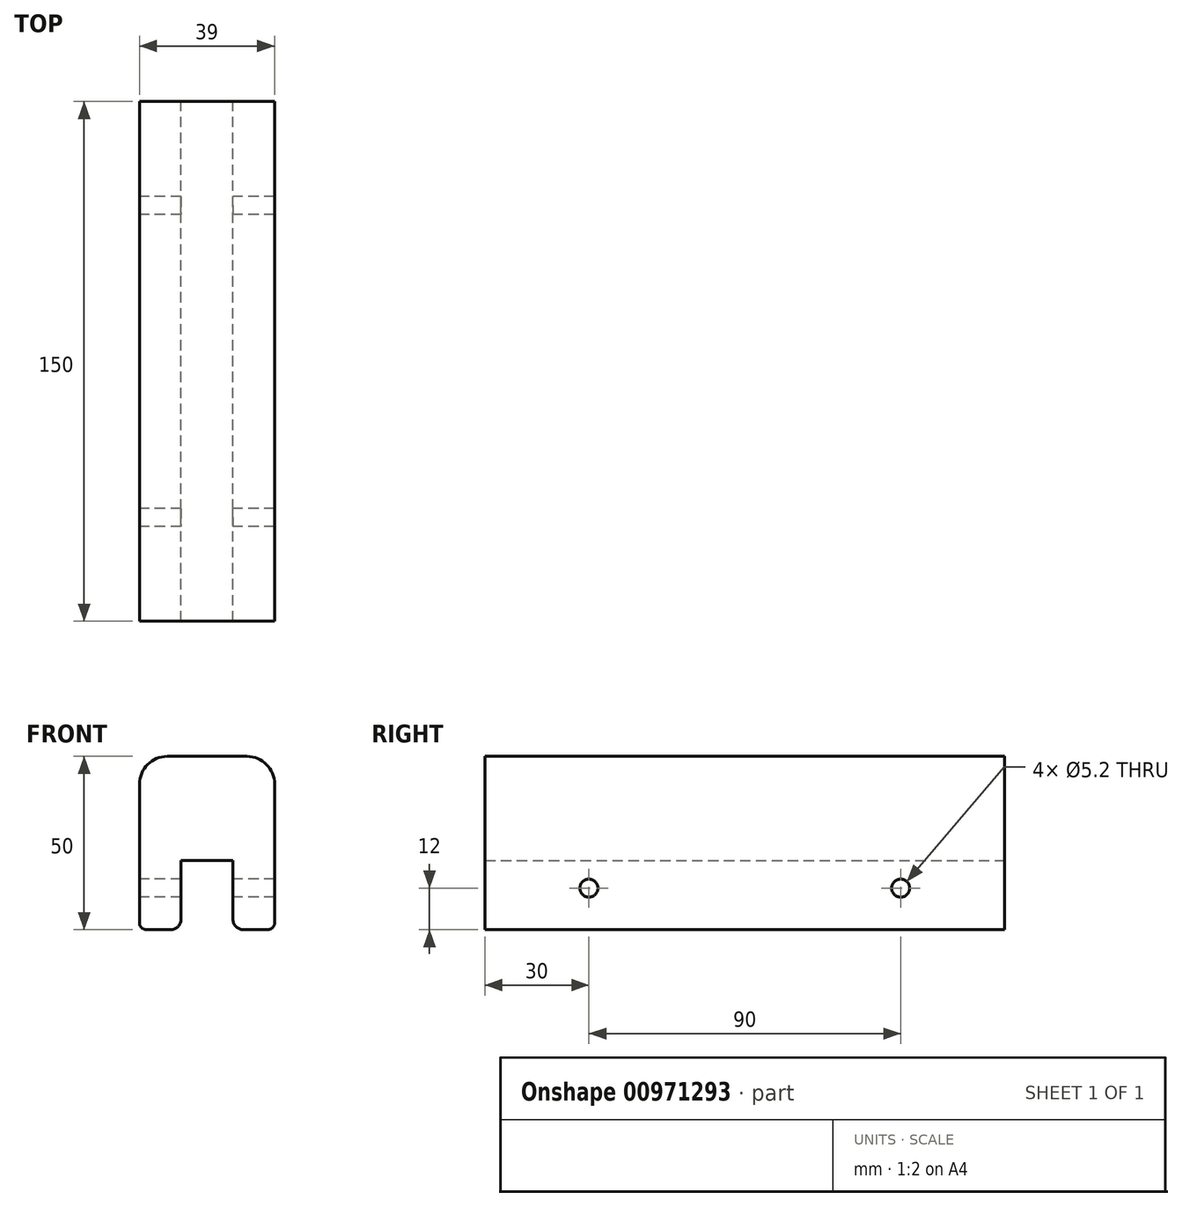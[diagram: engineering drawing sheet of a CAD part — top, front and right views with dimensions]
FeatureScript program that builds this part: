
annotation { "Feature Type Name" : "Feature", "Feature Type Description" : "" }
export const myFeature = defineFeature(function(context is Context, id is Id, definition is map)
    precondition{}
    {
        {
            var Q0;
            Q0=qCreatedBy(makeId("Front.planeOp"),FACE);
            var sketch = newSketch(context, id + "F0", { "sketchPlane" : qUnion([Q0])});
            skLineSegment(sketch, "E0", {"start": v(-20.24, 0) * mm, "end": v(-8.24, 0) * mm});
            skLineSegment(sketch, "E1", {"start": v(-8.24, 0) * mm, "end": v(-8.24, 20) * mm});
            skLineSegment(sketch, "E2", {"start": v(-8.24, 20) * mm, "end": v(6.76, 20) * mm});
            skLineSegment(sketch, "E3", {"start": v(6.76, 20) * mm, "end": v(6.76, 0) * mm});
            skLineSegment(sketch, "E4", {"start": v(6.76, 0) * mm, "end": v(18.76, 0) * mm});
            skLineSegment(sketch, "E5", {"start": v(18.76, 0) * mm, "end": v(18.76, 50) * mm});
            skLineSegment(sketch, "E6", {"start": v(18.76, 50) * mm, "end": v(-20.24, 50) * mm});
            skLineSegment(sketch, "E7", {"start": v(-20.24, 50) * mm, "end": v(-20.24, 0) * mm});
            skSolve(sketch);
        }
        {
            var Q0;
            Q0=makeQuery(id+"F0.imprint","IMPRINT",FACE,{"disambiguationData":[TD([[makeQuery(id+"F0.imprint","IMPRINT",EDGE,{"derivedFrom":sQuery(id+"F0.wireOp",EDGE,"E0")}),1.0]])]});
            extrude(context, id + "F1", {"entities" : qUnion([Q0]), "depth" : 150 * mm, "offsetDistance" : 25 * mm});
        }
        {
            var Q0;
            Q0=makeQuery(id+"F1.opExtrude","SWEPT_EDGE",EDGE,{"disambiguationData":[OSD([sQuery(id+"F0.wireOp",EDGE,"E0"),sQuery(id+"F0.wireOp",EDGE,"E1")])]});
            var Q1;
            Q1=makeQuery(id+"F1.opExtrude","SWEPT_EDGE",EDGE,{"disambiguationData":[OSD([sQuery(id+"F0.wireOp",EDGE,"E3"),sQuery(id+"F0.wireOp",EDGE,"E4")])]});
            fillet(context, id + "F2", {"entities" : qUnion([Q0, Q1]), "radius" : 3 * mm, "tangentPropagation" : true, "allowEdgeOverflow" : false});
        }
        {
            var Q0;
            Q0=makeQuery(id+"F1.opExtrude","SWEPT_EDGE",EDGE,{"disambiguationData":[OSD([sQuery(id+"F0.wireOp",EDGE,"E6"),sQuery(id+"F0.wireOp",EDGE,"E7")])]});
            var Q1;
            Q1=makeQuery(id+"F1.opExtrude","SWEPT_EDGE",EDGE,{"disambiguationData":[OSD([sQuery(id+"F0.wireOp",EDGE,"E5"),sQuery(id+"F0.wireOp",EDGE,"E6")])]});
            fillet(context, id + "F3", {"entities" : qUnion([Q0, Q1]), "radius" : 8 * mm, "tangentPropagation" : true, "allowEdgeOverflow" : false});
        }
        {
            var Q0;
            Q0=makeQuery(id+"F1.opExtrude","SWEPT_EDGE",EDGE,{"disambiguationData":[OSD([sQuery(id+"F0.wireOp",EDGE,"E4"),sQuery(id+"F0.wireOp",EDGE,"E5")])]});
            var Q1;
            Q1=makeQuery(id+"F1.opExtrude","SWEPT_EDGE",EDGE,{"disambiguationData":[OSD([sQuery(id+"F0.wireOp",EDGE,"E0"),sQuery(id+"F0.wireOp",EDGE,"E7")])]});
            fillet(context, id + "F4", {"entities" : qUnion([Q0, Q1]), "radius" : 2 * mm, "tangentPropagation" : true, "allowEdgeOverflow" : false});
        }
        {
            var Q0;
            Q0=makeQuery(id+"F1.opExtrude","SWEPT_FACE",FACE,{"disambiguationData":[OSD([sQuery(id+"F0.wireOp",EDGE,"E7")])]});
            var sketch = newSketch(context, id + "F5", { "sketchPlane" : qUnion([Q0])});
            skCircle(sketch, "E8", {"center": v(30, 12) * mm, "radius": 2.6 * mm});
            skCircle(sketch, "E9.1.0.0", {"center": v(120, 12) * mm, "radius": 2.6 * mm});
            skLineSegment(sketch, "E9.direction1", {"start": v(30, 12) * mm, "end": v(120, 12) * mm, "construction": true});
            skSolve(sketch);
        }
        {
            var Q0;
            Q0=makeQuery(id+"F5.imprint","IMPRINT",FACE,{"disambiguationData":[TD([[makeQuery(id+"F5.imprint","IMPRINT",EDGE,{"derivedFrom":sQuery(id+"F5.wireOp",EDGE,"E8")}),1.0]])]});
            var Q1;
            Q1=makeQuery(id+"F5.imprint","IMPRINT",FACE,{"disambiguationData":[TD([[makeQuery(id+"F5.imprint","IMPRINT",EDGE,{"derivedFrom":sQuery(id+"F5.wireOp",EDGE,"E9.1.0.0")}),1.0]])]});
            var Q2;
            Q2=sQuery(id+"F5.wireOp",EDGE,"E8");
            var Q3;
            Q3=makeQuery(id+"F1.opExtrude","SWEPT_FACE",FACE,{"disambiguationData":[OSD([sQuery(id+"F0.wireOp",EDGE,"E5")])]});
            var Q4;
            Q4=makeQuery(id+"F1.opExtrude","SWEPT_BODY",BODY,{"disambiguationData":[OSD([sQuery(id+"F0.wireOp",EDGE,"E0"),sQuery(id+"F0.wireOp",EDGE,"E1"),sQuery(id+"F0.wireOp",EDGE,"E2"),sQuery(id+"F0.wireOp",EDGE,"E3"),sQuery(id+"F0.wireOp",EDGE,"E4"),sQuery(id+"F0.wireOp",EDGE,"E5"),sQuery(id+"F0.wireOp",EDGE,"E6"),sQuery(id+"F0.wireOp",EDGE,"E7")])]});
            var Q5;
            Q5=makeQuery(id+"F1.opExtrude","SWEPT_FACE",FACE,{"disambiguationData":[OSD([sQuery(id+"F0.wireOp",EDGE,"E5")])]});
            extrude(context, id + "F6", {"entities" : qUnion([Q0, Q1]), "operationType" : NewBodyOperationType.REMOVE, "surfaceEntities" : qUnion([Q2]), "endBound" : BoundingType.UP_TO_SURFACE, "oppositeDirection" : true, "depth" : 25 * mm, "endBoundEntityFace" : qUnion([Q3]), "endBoundEntityBody" : qUnion([Q4]), "offsetDistance" : 25 * mm});
        }
    });
